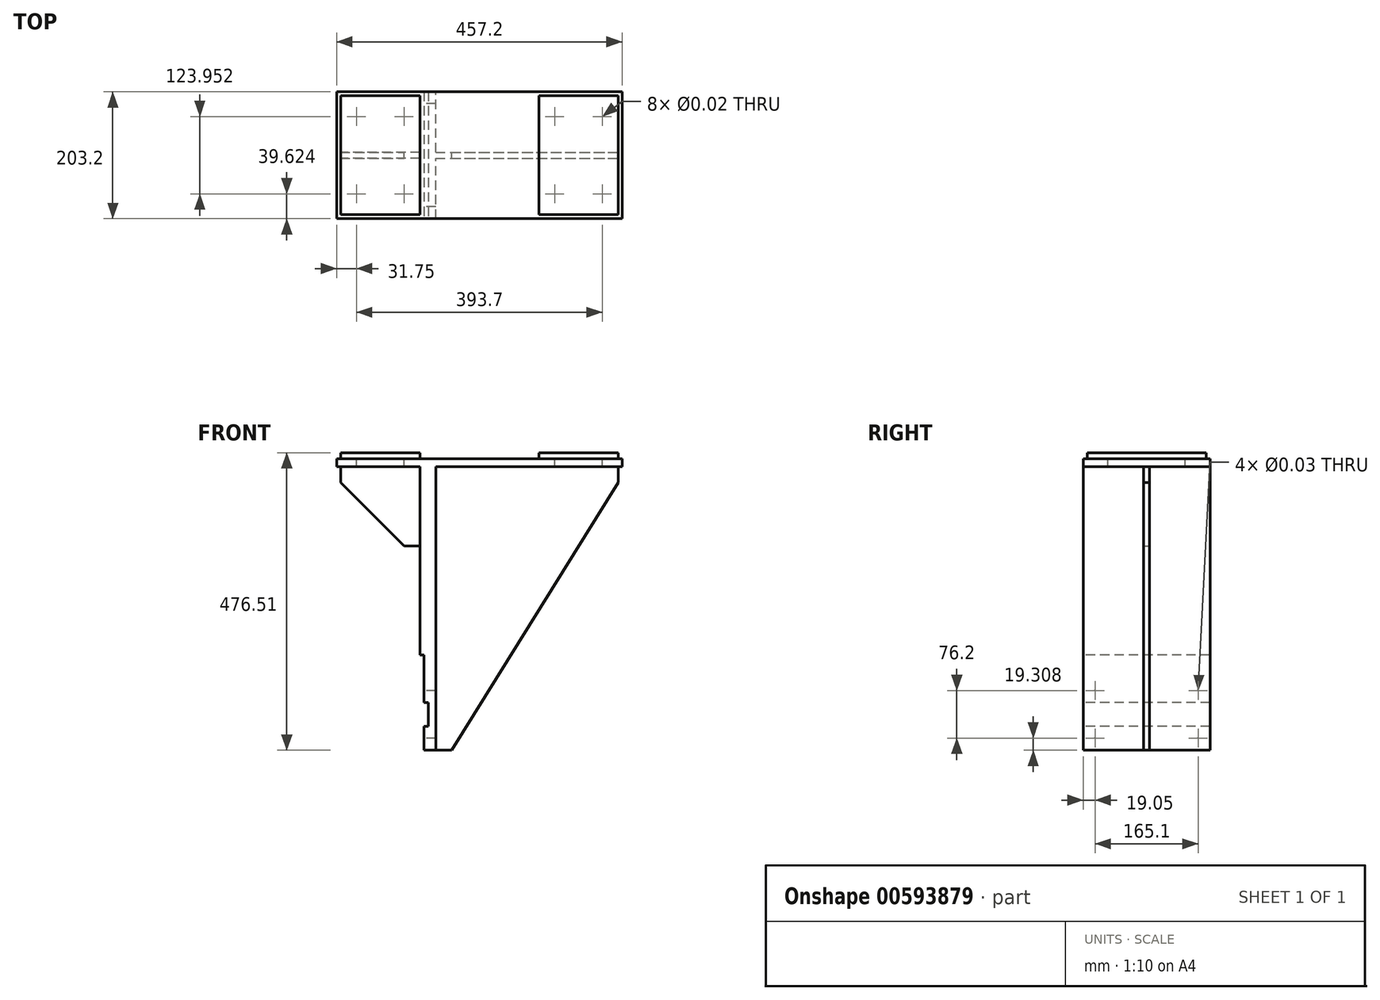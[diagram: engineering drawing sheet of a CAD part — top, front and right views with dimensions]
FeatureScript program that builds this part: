
annotation { "Feature Type Name" : "Feature", "Feature Type Description" : "" }
export const myFeature = defineFeature(function(context is Context, id is Id, definition is map)
    precondition{}
    {
        {
            var Q0;
            Q0=qCreatedBy(makeId("Right.planeOp"),FACE);
            var sketch = newSketch(context, id + "F0", { "sketchPlane" : qUnion([Q0])});
            skLineSegment(sketch, "E0.bottom", {"start": v(-101.6, 227.08) * mm, "end": v(101.6, 227.08) * mm});
            skLineSegment(sketch, "E0.top", {"start": v(-101.6, -227.08) * mm, "end": v(101.6, -227.08) * mm});
            skLineSegment(sketch, "E0.left", {"start": v(-101.6, 227.08) * mm, "end": v(-101.6, -227.08) * mm});
            skLineSegment(sketch, "E0.right", {"start": v(101.6, 227.08) * mm, "end": v(101.6, -227.08) * mm});
            skPoint(sketch, "E0.middle", {"position": v(0, 0) * mm});
            skSolve(sketch);
        }
        {
            var Q0;
            Q0 = qSketchRegion(id + "F0", true);
            extrude(context, id + "F1", {"entities" : qUnion([Q0]), "depth" : 25.4 * mm, "offsetDistance" : 25.4 * mm});
        }
        {
            var Q0;
            Q0=makeQuery(id+"F1.opExtrude","SWEPT_FACE",FACE,{"disambiguationData":[OSD([sQuery(id+"F0.wireOp",EDGE,"E0.left")])]});
            var sketch = newSketch(context, id + "F2", { "sketchPlane" : qUnion([Q0])});
            skLineSegment(sketch, "E1.bottom", {"start": v(0, -227.08) * mm, "end": v(6.35, -227.08) * mm});
            skLineSegment(sketch, "E1.top", {"start": v(0, -74.68) * mm, "end": v(6.35, -74.68) * mm});
            skLineSegment(sketch, "E1.left", {"start": v(0, -227.08) * mm, "end": v(0, -74.68) * mm});
            skLineSegment(sketch, "E1.right", {"start": v(6.35, -227.08) * mm, "end": v(6.35, -74.68) * mm});
            skSolve(sketch);
        }
        {
            var Q0;
            Q0 = qSketchRegion(id + "F2", true);
            extrude(context, id + "F3", {"entities" : qUnion([Q0]), "operationType" : NewBodyOperationType.REMOVE, "endBound" : BoundingType.THROUGH_ALL, "oppositeDirection" : true, "depth" : 25.4 * mm, "offsetDistance" : 25.4 * mm});
        }
        {
            var Q0;
            Q0=makeQuery(id+"F1.opExtrude","SWEPT_FACE",FACE,{"disambiguationData":[OSD([sQuery(id+"F0.wireOp",EDGE,"E0.bottom")])]});
            var sketch = newSketch(context, id + "F4", { "sketchPlane" : qUnion([Q0])});
            skLineSegment(sketch, "E2.0", {"start": v(323.85, -101.6) * mm, "end": v(323.85, 101.6) * mm});
            skLineSegment(sketch, "E3.0", {"start": v(-133.35, -101.6) * mm, "end": v(-133.35, 101.6) * mm});
            skLineSegment(sketch, "E4", {"start": v(-133.35, 101.6) * mm, "end": v(323.85, 101.6) * mm});
            skLineSegment(sketch, "E5", {"start": v(-133.35, -101.6) * mm, "end": v(323.85, -101.6) * mm});
            skSolve(sketch);
        }
        {
            var Q0;
            Q0 = qSketchRegion(id + "F4", true);
            extrude(context, id + "F5", {"entities" : qUnion([Q0]), "operationType" : NewBodyOperationType.ADD, "depth" : 12.7 * mm, "offsetDistance" : 25.4 * mm});
        }
        {
            var Q0;
            Q0=makeQuery(id+"F5.opExtrude","CAP_FACE",FACE,{"disambiguationData":[OSD([sQuery(id+"F4.wireOp",EDGE,"E2.0"),sQuery(id+"F4.wireOp",EDGE,"E3.0"),sQuery(id+"F4.wireOp",EDGE,"E4"),sQuery(id+"F4.wireOp",EDGE,"E5")])],"isStart":false});
            var sketch = newSketch(context, id + "F6", { "sketchPlane" : qUnion([Q0])});
            skLineSegment(sketch, "E6.0", {"start": v(-127, -101.6) * mm, "end": v(-127, 101.6) * mm});
            skLineSegment(sketch, "E7.0", {"start": v(0, -101.6) * mm, "end": v(0, 101.6) * mm});
            skLineSegment(sketch, "E8.0", {"start": v(190.5, -101.6) * mm, "end": v(190.5, 101.6) * mm});
            skLineSegment(sketch, "E9.0", {"start": v(317.5, -101.6) * mm, "end": v(317.5, 101.6) * mm});
            skLineSegment(sketch, "E10.0", {"start": v(-133.35, -95.25) * mm, "end": v(0, -95.25) * mm});
            skLineSegment(sketch, "E11.0", {"start": v(-133.35, 95.25) * mm, "end": v(0, 95.25) * mm});
            skLineSegment(sketch, "E12.trimOffspring", {"start": v(190.5, 95.25) * mm, "end": v(323.85, 95.25) * mm});
            skLineSegment(sketch, "E13.trimOffspring", {"start": v(190.5, -95.25) * mm, "end": v(323.85, -95.25) * mm});
            skSolve(sketch);
        }
        {
            var Q0;
            Q0 = qSketchRegion(id + "F6", true);
            extrude(context, id + "F7", {"entities" : qUnion([Q0]), "depth" : 9.65 * mm, "offsetDistance" : 25.4 * mm});
        }
        {
            var Q0;
            Q0=makeQuery(id+"F7.opExtrude","CAP_FACE",FACE,{"disambiguationData":[OSD([sQuery(id+"F6.wireOp",EDGE,"E8.0"),sQuery(id+"F6.wireOp",EDGE,"E9.0"),sQuery(id+"F6.wireOp",EDGE,"E12.trimOffspring"),sQuery(id+"F6.wireOp",EDGE,"E13.trimOffspring")])],"isStart":false});
            var sketch = newSketch(context, id + "F8", { "sketchPlane" : qUnion([Q0])});
            skLineSegment(sketch, "E14", {"start": v(254, 95.25) * mm, "end": v(254, -95.25) * mm, "construction": true});
            skLineSegment(sketch, "E15.0", {"start": v(-127, 95.25) * mm, "end": v(0, 95.25) * mm, "construction": true});
            skLineSegment(sketch, "E16.0", {"start": v(-127, -95.25) * mm, "end": v(0, -95.25) * mm, "construction": true});
            skLineSegment(sketch, "E17.0", {"start": v(317.5, -95.25) * mm, "end": v(317.5, 95.25) * mm, "construction": true});
            skLineSegment(sketch, "E18", {"start": v(-63.5, -95.25) * mm, "end": v(-63.5, 95.25) * mm, "construction": true});
            skLineSegment(sketch, "E19", {"start": v(317.5, 0) * mm, "end": v(-144.3, 0) * mm, "construction": true});
            skLineSegment(sketch, "E20.0", {"start": v(-25.4, -95.25) * mm, "end": v(-25.4, 95.25) * mm, "construction": true});
            skLineSegment(sketch, "E21.0", {"start": v(215.9, 95.25) * mm, "end": v(215.9, -95.25) * mm, "construction": true});
            skLineSegment(sketch, "E22.0", {"start": v(317.5, 61.98) * mm, "end": v(-144.3, 61.98) * mm, "construction": true});
            skPoint(sketch, "E23", {"position": v(-25.4, 61.98) * mm});
            skPoint(sketch, "E24", {"position": v(215.9, 61.98) * mm});
            skPoint(sketch, "E25.0.1.0", {"position": v(215.9, -61.98) * mm});
            skPoint(sketch, "E25.1.0.0", {"position": v(292.1, 61.98) * mm});
            skPoint(sketch, "E25.1.1.0", {"position": v(292.1, -61.98) * mm});
            skLineSegment(sketch, "E25.direction1", {"start": v(215.9, 61.98) * mm, "end": v(292.1, 61.98) * mm, "construction": true});
            skLineSegment(sketch, "E25.direction2", {"start": v(215.9, 61.98) * mm, "end": v(215.9, -61.98) * mm, "construction": true});
            skPoint(sketch, "E26.0.1.0", {"position": v(-25.4, -61.98) * mm});
            skPoint(sketch, "E26.1.0.0", {"position": v(-101.6, 61.98) * mm});
            skPoint(sketch, "E26.1.1.0", {"position": v(-101.6, -61.98) * mm});
            skLineSegment(sketch, "E26.direction1", {"start": v(-25.4, 61.98) * mm, "end": v(-101.6, 61.98) * mm, "construction": true});
            skLineSegment(sketch, "E26.direction2", {"start": v(-25.4, 61.98) * mm, "end": v(-25.4, -61.98) * mm, "construction": true});
            skSolve(sketch);
        }
        {
            var Q0;
            Q0=sQuery(id+"F8.wireOp",VERTEX,"E26.1.0.0");
            var Q1;
            Q1=sQuery(id+"F8.wireOp",VERTEX,"E23");
            var Q2;
            Q2=sQuery(id+"F8.wireOp",VERTEX,"E26.1.1.0");
            var Q3;
            Q3=sQuery(id+"F8.wireOp",VERTEX,"E26.0.1.0");
            var Q4;
            Q4=sQuery(id+"F8.wireOp",VERTEX,"E24");
            var Q5;
            Q5=sQuery(id+"F8.wireOp",VERTEX,"E25.1.0.0");
            var Q6;
            Q6=sQuery(id+"F8.wireOp",VERTEX,"E25.0.1.0");
            var Q7;
            Q7=sQuery(id+"F8.wireOp",VERTEX,"E25.1.1.0");
            var Q8;
            Q8=makeQuery(id+"F1.opExtrude","SWEPT_BODY",BODY,{"disambiguationData":[OSD([sQuery(id+"F0.wireOp",EDGE,"E0.bottom"),sQuery(id+"F0.wireOp",EDGE,"E0.top"),sQuery(id+"F0.wireOp",EDGE,"E0.left"),sQuery(id+"F0.wireOp",EDGE,"E0.right")])]});
            hole(context, id + "F9", {"style" : HoleStyle.SIMPLE, "endStyle" : HoleEndStyle.THROUGH, "standardTappedOrClearance" : lookupTablePath({ "standard" : "ANSI", "size" : "7/16 (0.44)", "type" : "Drilled" }), "standardBlindInLast" : lookupTablePath({ "standard" : "ANSI", "size" : "7/16", "type" : "Drilled" }), "holeDiameter" : 7 / 406.4 * mm, "majorDiameter" : 12.7 * mm, "isTappedThrough" : true, "tappedDepth" : 25.4 * mm, "tapClearance" : 3, "locations" : qUnion([Q0, Q1, Q2, Q3, Q4, Q5, Q6, Q7]), "scope" : qUnion([Q8])});
        }
        {
            var Q0;
            Q0=qCreatedBy(makeId("Front.planeOp"),FACE);
            var sketch = newSketch(context, id + "F10", { "sketchPlane" : qUnion([Q0])});
            skLineSegment(sketch, "E27.0", {"start": v(25.4, 227.08) * mm, "end": v(323.85, 227.08) * mm});
            skLineSegment(sketch, "E28.0", {"start": v(25.4, 227.08) * mm, "end": v(25.4, -227.08) * mm});
            skLineSegment(sketch, "E29.0", {"start": v(25.4, 201.68) * mm, "end": v(323.85, 201.68) * mm, "construction": true});
            skLineSegment(sketch, "E30.0", {"start": v(50.8, 227.08) * mm, "end": v(50.8, -227.08) * mm, "construction": true});
            skLineSegment(sketch, "E31", {"start": v(323.85, 227.08) * mm, "end": v(323.85, 95.77) * mm, "construction": true});
            skLineSegment(sketch, "E32.0", {"start": v(317.5, 227.08) * mm, "end": v(317.5, 201.68) * mm});
            skLineSegment(sketch, "E33", {"start": v(25.4, -227.08) * mm, "end": v(50.8, -227.08) * mm});
            skLineSegment(sketch, "E34", {"start": v(50.8, -227.08) * mm, "end": v(317.5, 201.68) * mm});
            skSolve(sketch);
        }
        {
            var Q0;
            Q0 = qSketchRegion(id + "F10", true);
            extrude(context, id + "F11", {"entities" : qUnion([Q0]), "operationType" : NewBodyOperationType.ADD, "endBound" : BoundingType.SYMMETRIC, "depth" : 9.52 * mm, "offsetDistance" : 25.4 * mm});
        }
        {
            var Q0;
            Q0=makeQuery(id+"F5.boolean.opBoolean","MERGE",FACE,{"derivedFrom":[makeQuery(id+"F1.opExtrude","SWEPT_FACE",FACE,{"disambiguationData":[OSD([sQuery(id+"F0.wireOp",EDGE,"E0.left")])]}),makeQuery(id+"F5.opExtrude","SWEPT_FACE",FACE,{"disambiguationData":[OSD([sQuery(id+"F4.wireOp",EDGE,"E5")])]})]});
            var sketch = newSketch(context, id + "F12", { "sketchPlane" : qUnion([Q0])});
            skLineSegment(sketch, "E35.0", {"start": v(-127, 249.43) * mm, "end": v(0, 249.43) * mm, "construction": true});
            skLineSegment(sketch, "E36.0", {"start": v(-127, -169.67) * mm, "end": v(0, -169.67) * mm, "construction": true});
            skLineSegment(sketch, "E37.0", {"start": v(-127, -188.72) * mm, "end": v(13.2, -188.72) * mm, "construction": true});
            skLineSegment(sketch, "E38.0", {"start": v(13.2, -227.08) * mm, "end": v(13.2, -74.68) * mm, "construction": true});
            skLineSegment(sketch, "E39.bottom", {"start": v(13.2, -188.72) * mm, "end": v(-24.9, -188.72) * mm});
            skLineSegment(sketch, "E39.top", {"start": v(13.2, -150.62) * mm, "end": v(-24.9, -150.62) * mm});
            skLineSegment(sketch, "E39.left", {"start": v(13.2, -188.72) * mm, "end": v(13.2, -150.62) * mm});
            skLineSegment(sketch, "E39.right", {"start": v(-24.9, -188.72) * mm, "end": v(-24.9, -150.62) * mm});
            skSolve(sketch);
        }
        {
            var Q0;
            Q0 = qSketchRegion(id + "F12", true);
            extrude(context, id + "F13", {"entities" : qUnion([Q0]), "operationType" : NewBodyOperationType.REMOVE, "endBound" : BoundingType.THROUGH_ALL, "oppositeDirection" : true, "depth" : 25.4 * mm, "offsetDistance" : 25.4 * mm});
        }
        {
            var Q0;
            Q0=makeQuery(id+"F13.boolean.opBoolean","SPLIT",FACE,{"disambiguationData":[TD([makeQuery(id+"F3.boolean.opBoolean","COPY",FACE,{"derivedFrom":makeQuery(id+"F3.opExtrude","SWEPT_FACE",FACE,{"disambiguationData":[OSD([sQuery(id+"F2.wireOp",EDGE,"E1.top")])]})})])],"derivedFrom":makeQuery(id+"F3.boolean.opBoolean","COPY",FACE,{"derivedFrom":makeQuery(id+"F3.opExtrude","SWEPT_FACE",FACE,{"disambiguationData":[OSD([sQuery(id+"F2.wireOp",EDGE,"E1.right")])]})})});
            var sketch = newSketch(context, id + "F14", { "sketchPlane" : qUnion([Q0])});
            skLineSegment(sketch, "E40.0", {"start": v(95.25, -169.67) * mm, "end": v(-95.25, -169.67) * mm, "construction": true});
            skLineSegment(sketch, "E41.0", {"start": v(95.25, -207.77) * mm, "end": v(-95.25, -207.77) * mm, "construction": true});
            skLineSegment(sketch, "E42", {"start": v(0, 289.27) * mm, "end": v(0, -288.68) * mm, "construction": true});
            skPoint(sketch, "E42.endSnap0", {"position": v(0, -207.77) * mm});
            skLineSegment(sketch, "E43.0", {"start": v(-82.55, 289.27) * mm, "end": v(-82.55, -288.68) * mm, "construction": true});
            skPoint(sketch, "E44", {"position": v(-82.55, -207.77) * mm});
            skPoint(sketch, "E45.0.1.0", {"position": v(-82.55, -131.57) * mm});
            skPoint(sketch, "E45.1.0.0", {"position": v(82.55, -207.77) * mm});
            skPoint(sketch, "E45.1.1.0", {"position": v(82.55, -131.57) * mm});
            skLineSegment(sketch, "E45.direction1", {"start": v(-82.55, -207.77) * mm, "end": v(82.55, -207.77) * mm, "construction": true});
            skLineSegment(sketch, "E45.direction2", {"start": v(-82.55, -207.77) * mm, "end": v(-82.55, -131.57) * mm, "construction": true});
            skSolve(sketch);
        }
        {
            var Q0;
            Q0=sQuery(id+"F14.wireOp",VERTEX,"E45.0.1.0");
            var Q1;
            Q1=sQuery(id+"F14.wireOp",VERTEX,"E45.1.1.0");
            var Q2;
            Q2=sQuery(id+"F14.wireOp",VERTEX,"E45.1.0.0");
            var Q3;
            Q3=sQuery(id+"F14.wireOp",VERTEX,"E44");
            var Q4;
            Q4=makeQuery(id+"F1.opExtrude","SWEPT_BODY",BODY,{"disambiguationData":[OSD([sQuery(id+"F0.wireOp",EDGE,"E0.bottom"),sQuery(id+"F0.wireOp",EDGE,"E0.top"),sQuery(id+"F0.wireOp",EDGE,"E0.left"),sQuery(id+"F0.wireOp",EDGE,"E0.right")])]});
            hole(context, id + "F15", {"style" : HoleStyle.SIMPLE, "endStyle" : HoleEndStyle.THROUGH, "standardTappedOrClearance" : lookupTablePath({ "standard" : "ANSI", "size" : "11/16 (0.69)", "type" : "Drilled" }), "standardBlindInLast" : lookupTablePath({ "standard" : "ANSI", "size" : "11/16", "type" : "Drilled" }), "holeDiameter" : 11 / 406.4 * mm, "majorDiameter" : 6.35 * mm, "isTappedThrough" : true, "tappedDepth" : 25.4 * mm, "tapClearance" : 3, "locations" : qUnion([Q0, Q1, Q2, Q3]), "scope" : qUnion([Q4])});
        }
        {
            var Q0;
            Q0=qCreatedBy(makeId("Front.planeOp"),FACE);
            var sketch = newSketch(context, id + "F16", { "sketchPlane" : qUnion([Q0])});
            skLineSegment(sketch, "E46.0", {"start": v(-133.35, 227.08) * mm, "end": v(0, 227.08) * mm, "construction": true});
            skLineSegment(sketch, "E47.bottom", {"start": v(0, 227.08) * mm, "end": v(-127, 227.08) * mm});
            skLineSegment(sketch, "E47.top", {"start": v(0, 100.08) * mm, "end": v(-127, 100.08) * mm});
            skLineSegment(sketch, "E47.left", {"start": v(0, 227.08) * mm, "end": v(0, 100.08) * mm});
            skLineSegment(sketch, "E47.right", {"start": v(-127, 227.08) * mm, "end": v(-127, 201.68) * mm});
            skLineSegment(sketch, "E48.bottom", {"start": v(-127, 100.08) * mm, "end": v(-25.4, 100.08) * mm, "construction": true});
            skLineSegment(sketch, "E48.top", {"start": v(-127, 201.68) * mm, "end": v(-25.4, 201.68) * mm, "construction": true});
            skLineSegment(sketch, "E48.right", {"start": v(-25.4, 100.08) * mm, "end": v(-25.4, 201.68) * mm, "construction": true});
            skLineSegment(sketch, "E49", {"start": v(-127, 201.68) * mm, "end": v(-25.4, 100.08) * mm});
            skSolve(sketch);
        }
        {
            var Q0;
            Q0 = qSketchRegion(id + "F16", true);
            extrude(context, id + "F17", {"entities" : qUnion([Q0]), "operationType" : NewBodyOperationType.ADD, "endBound" : BoundingType.SYMMETRIC, "depth" : 9.65 * mm, "offsetDistance" : 25.4 * mm});
        }
    });
